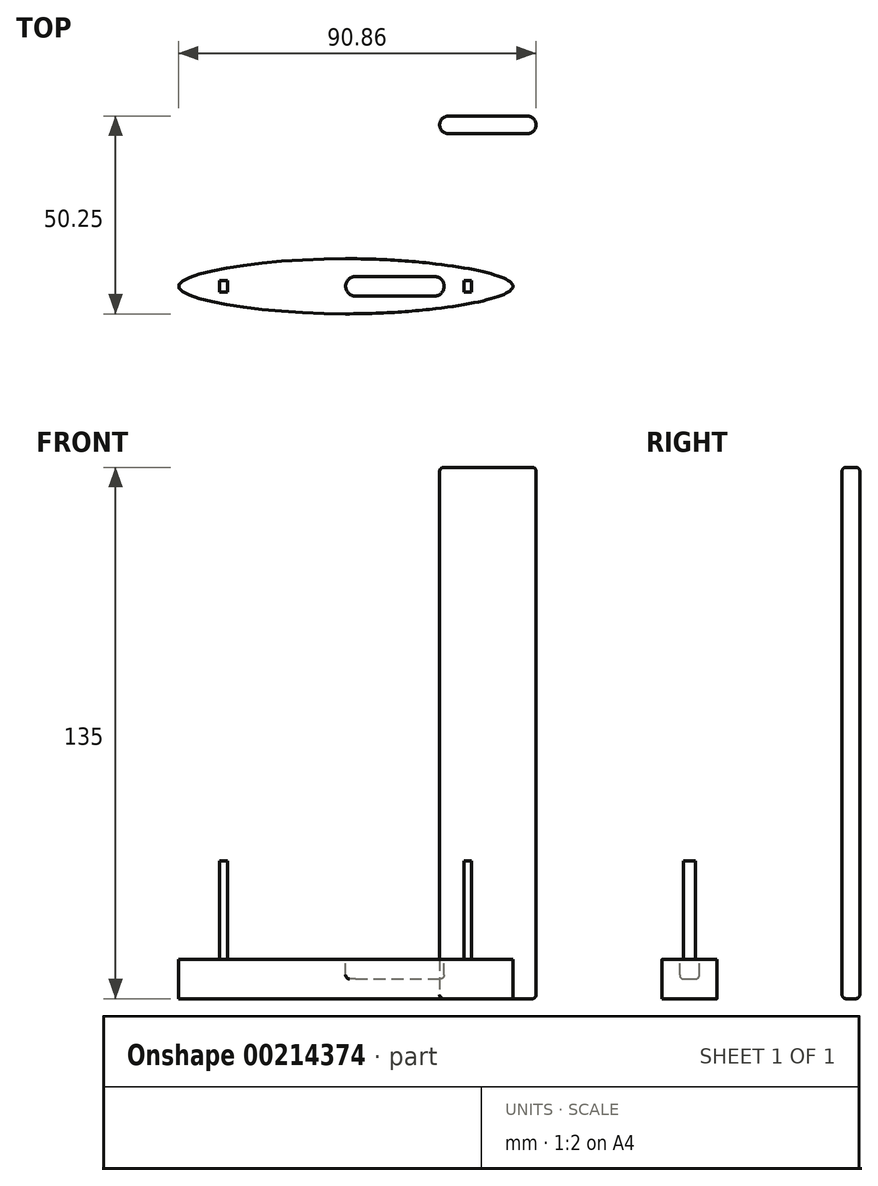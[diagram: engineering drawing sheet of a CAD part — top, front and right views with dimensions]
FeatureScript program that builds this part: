
annotation { "Feature Type Name" : "Feature", "Feature Type Description" : "" }
export const myFeature = defineFeature(function(context is Context, id is Id, definition is map)
    precondition{}
    {
        {
            var Q0;
            Q0=qCreatedBy(makeId("Top.planeOp"),FACE);
            var sketch = newSketch(context, id + "F0", { "sketchPlane" : qUnion([Q0])});
            skCircle(sketch, "E0", {"center": v(26.11, 41) * mm, "radius": 2.25 * mm});
            skCircle(sketch, "E1", {"center": v(46.11, 41) * mm, "radius": 2.25 * mm});
            skLineSegment(sketch, "E2", {"start": v(26.11, 43.25) * mm, "end": v(46.11, 43.25) * mm});
            skLineSegment(sketch, "E3", {"start": v(46.11, 38.75) * mm, "end": v(26.11, 38.75) * mm});
            skSolve(sketch);
        }
        {
            var Q0;
            Q0 = qSketchRegion(id + "F0", true);
            extrude(context, id + "F1", {"entities" : qUnion([Q0]), "depth" : 135 * mm});
        }
        {
            var Q0;
            Q0=makeQuery(id+"F1.opExtrude","CAP_FACE",FACE,{"disambiguationData":[OSD([sQuery(id+"F0.wireOp",EDGE,"E0"),sQuery(id+"F0.wireOp",EDGE,"E1"),sQuery(id+"F0.wireOp",EDGE,"E2"),sQuery(id+"F0.wireOp",EDGE,"E3")])],"isStart":true});
            var Q1;
            Q1=makeQuery(id+"F1.opExtrude","CAP_FACE",FACE,{"disambiguationData":[OSD([sQuery(id+"F0.wireOp",EDGE,"E0"),sQuery(id+"F0.wireOp",EDGE,"E1"),sQuery(id+"F0.wireOp",EDGE,"E2"),sQuery(id+"F0.wireOp",EDGE,"E3")])],"isStart":false});
            fillet(context, id + "F2", {"entities" : qUnion([Q0, Q1]), "radius" : 1 * mm, "tangentPropagation" : true, "allowEdgeOverflow" : false});
        }
        {
            var Q0;
            Q0=qCreatedBy(makeId("Top.planeOp"),FACE);
            var sketch = newSketch(context, id + "F3", { "sketchPlane" : qUnion([Q0])});
            skFitSpline(sketch, "E4", {"points": [v(0, -7) * mm, v(42.5, 0) * mm, v(0, 7) * mm], "startDerivative": vector(127.5, 0) * mm, "endDerivative": vector(-127.5, 0) * mm});
            skLineSegment(sketch, "E5", {"start": v(0, 7) * mm, "end": v(0, -7) * mm});
            skLineSegment(sketch, "E6", {"start": v(0, 0) * mm, "end": v(21.25, 0) * mm});
            skLineSegment(sketch, "E7", {"start": v(42.5, 0) * mm, "end": v(21.25, 0) * mm});
            skLineSegment(sketch, "E8", {"start": v(21.25, 7) * mm, "end": v(21.25, -7) * mm});
            skFitSpline(sketch, "E9.MirrorCS", {"points": [v(0, -7) * mm, v(-42.5, 0) * mm, v(0, 7) * mm], "startDerivative": vector(-127.5, 0) * mm, "endDerivative": vector(127.5, 0) * mm});
            skSolve(sketch);
        }
        {
            var Q0;
            Q0 = qSketchRegion(id + "F3", true);
            extrude(context, id + "F4", {"entities" : qUnion([Q0]), "depth" : 10 * mm});
        }
        {
            var Q0;
            Q0=makeQuery(id+"F4.opExtrude","CAP_FACE",FACE,{"disambiguationData":[OSD([sQuery(id+"F3.wireOp",EDGE,"E4"),sQuery(id+"F3.wireOp",EDGE,"E9.MirrorCS")])],"isStart":false});
            var sketch = newSketch(context, id + "F5", { "sketchPlane" : qUnion([Q0])});
            skCircle(sketch, "E10", {"center": v(2.5, 0) * mm, "radius": 2.5 * mm});
            skCircle(sketch, "E11", {"center": v(22.5, 0) * mm, "radius": 2.5 * mm});
            skLineSegment(sketch, "E12", {"start": v(2.5, 2.5) * mm, "end": v(22.5, 2.5) * mm});
            skLineSegment(sketch, "E13", {"start": v(22.5, -2.5) * mm, "end": v(2.5, -2.5) * mm});
            skSolve(sketch);
        }
        {
            var Q0;
            Q0 = qSketchRegion(id + "F5", true);
            extrude(context, id + "F6", {"entities" : qUnion([Q0]), "operationType" : NewBodyOperationType.REMOVE, "oppositeDirection" : true, "depth" : 5 * mm});
        }
        {
            var Q0;
            Q0=makeQuery(id+"F6.boolean.opBoolean","COPY",FACE,{"derivedFrom":makeQuery(id+"F6.opExtrude","CAP_FACE",FACE,{"disambiguationData":[OSD([sQuery(id+"F5.wireOp",EDGE,"E10"),sQuery(id+"F5.wireOp",EDGE,"E11"),sQuery(id+"F5.wireOp",EDGE,"E12"),sQuery(id+"F5.wireOp",EDGE,"E13")])],"isStart":false})});
            var Q1;
            Q1=makeQuery(id+"F6.boolean.opBoolean","COPY",EDGE,{"derivedFrom":makeQuery(id+"F6.opExtrude","CAP_EDGE",EDGE,{"disambiguationData":[OSD([sQuery(id+"F5.wireOp",EDGE,"E10")])],"isStart":true})});
            fillet(context, id + "F7", {"entities" : qUnion([Q0, Q1]), "radius" : 1 * mm, "tangentPropagation" : true, "allowEdgeOverflow" : false});
        }
        {
            var Q0;
            Q0=makeQuery(id+"F4.opExtrude","CAP_FACE",FACE,{"disambiguationData":[OSD([sQuery(id+"F3.wireOp",EDGE,"E4"),sQuery(id+"F3.wireOp",EDGE,"E9.MirrorCS")])],"isStart":false});
            var sketch = newSketch(context, id + "F8", { "sketchPlane" : qUnion([Q0])});
            skLineSegment(sketch, "E14.bottom", {"start": v(-32, -1.5) * mm, "end": v(-30, -1.5) * mm});
            skLineSegment(sketch, "E14.top", {"start": v(-32, 1.5) * mm, "end": v(-30, 1.5) * mm});
            skLineSegment(sketch, "E14.left", {"start": v(-32, -1.5) * mm, "end": v(-32, 1.5) * mm});
            skLineSegment(sketch, "E14.right", {"start": v(-30, -1.5) * mm, "end": v(-30, 1.5) * mm});
            skLineSegment(sketch, "E15.MirrorCS", {"start": v(30, -1.5) * mm, "end": v(30, 1.5) * mm});
            skLineSegment(sketch, "E16.MirrorCS", {"start": v(32, 1.5) * mm, "end": v(30, 1.5) * mm});
            skLineSegment(sketch, "E17.MirrorCS", {"start": v(32, -1.5) * mm, "end": v(32, 1.5) * mm});
            skLineSegment(sketch, "E18.MirrorCS", {"start": v(32, -1.5) * mm, "end": v(30, -1.5) * mm});
            skLineSegment(sketch, "E19", {"start": v(0, 0) * mm, "end": v(-30, 0) * mm});
            skSolve(sketch);
        }
        {
            var Q0;
            Q0 = qSketchRegion(id + "F8", true);
            extrude(context, id + "F9", {"entities" : qUnion([Q0]), "operationType" : NewBodyOperationType.ADD, "depth" : 25 * mm});
        }
    });
